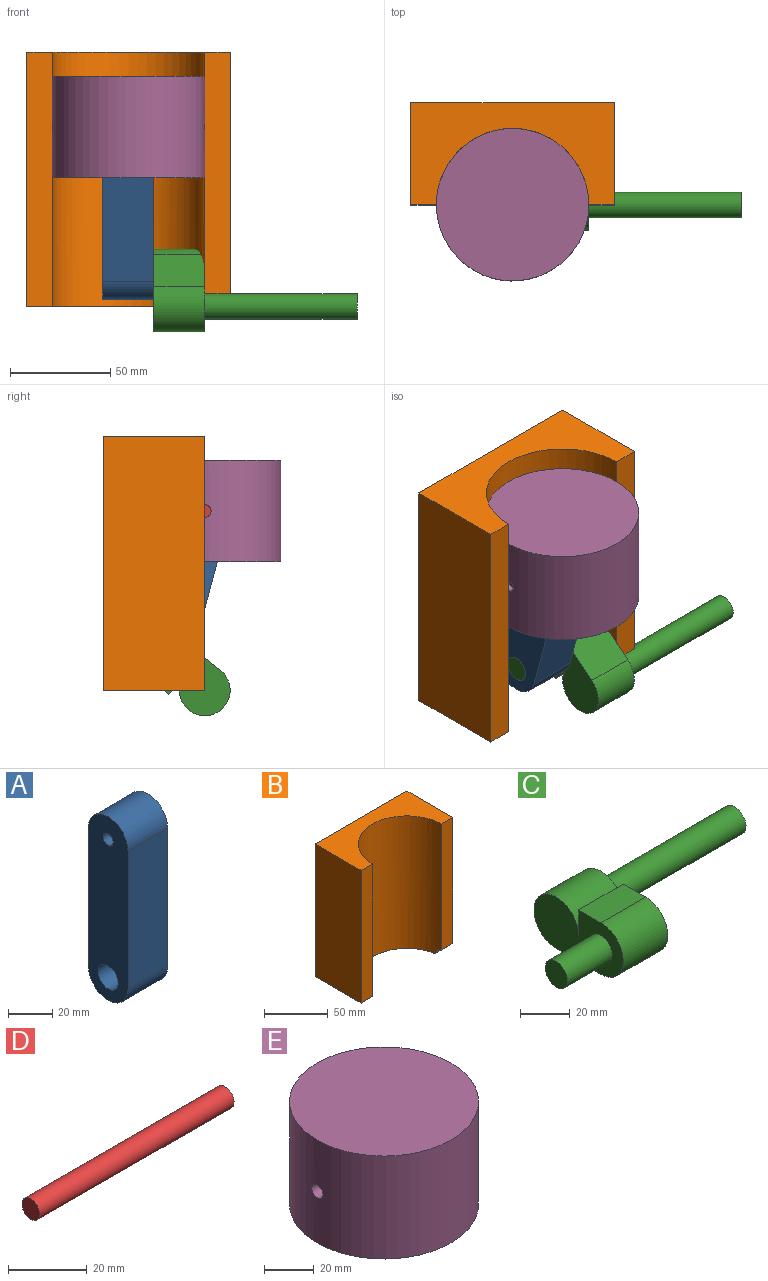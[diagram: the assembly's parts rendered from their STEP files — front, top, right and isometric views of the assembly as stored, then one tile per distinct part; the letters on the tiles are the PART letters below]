
ASSEMBLY  parts=5 mates=5
PART A: 8 faces, bbox 25.4x25.4x101.6 mm
  f0: plane 76.2x25.4mm, normal (0,1,0), area 1935.5mm2, adj f1,f4,f6,f7
  f1: cylinder r=12.7mm len=25.4mm, axis (1,0,0), area 1013.4mm2, adj f0,f2,f6,f7
  f2: plane 76.2x25.4mm, normal (0,-1,0), area 1935.5mm2, adj f1,f4,f6,f7
  f3: cylinder r=6.35mm len=25.4mm, axis (1,0,0), area 1013.4mm2, adj f6,f7
  f4: cylinder r=12.7mm len=25.4mm, axis (1,0,0), area 1013.4mm2, adj f0,f2,f6,f7
  f5: cylinder r=3.17mm len=25.4mm, axis (1,0,0), area 506.7mm2, adj f6,f7
  f6: plane 101.6x25.4mm, normal (-1,0,0), area 2283.8mm2, adj f0,f1,f2,f3,f4,f5
  f7: plane 101.6x25.4mm, normal (1,0,0), area 2283.8mm2, adj f0,f1,f2,f3,f4,f5
PART B: 10 faces, bbox 101.6x50.8x127 mm
  f0: cylinder r=38.1mm len=127mm, axis (0,0,1), area 15173mm2, adj f1,f2,f6,f7,f8
  f1: plane 120.65x12.7mm, normal (0,-1,0), area 1532.3mm2, adj f0,f3,f7,f9
  f2: plane 101.6x50.8mm, normal (0,0,-1), area 2799.5mm2, adj f0,f3,f4,f5,f6,f8,f9
  f3: plane 127x50.8mm, normal (1,0,0), area 6419.9mm2, adj f1,f2,f4,f7,f9
  f4: plane 127x101.6mm, normal (0,1,0), area 12903.2mm2, adj f2,f3,f5,f7
  f5: plane 127x50.8mm, normal (-1,0,0), area 6451.6mm2, adj f2,f4,f6,f7
  f6: plane 127x12.7mm, normal (0,-1,0), area 1612.9mm2, adj f0,f2,f5,f7
  f7: plane 101.6x50.8mm, normal (0,0,1), area 2881.1mm2, adj f0,f1,f3,f4,f5,f6
  f8: cone r=0mm half-angle=59deg, axis (1,0,0), area 4.1mm2, adj f0,f2,f9
  f9: cylinder r=6.35mm len=12.7mm, axis (1,0,0), area 126.7mm2, adj f1,f2,f3,f8
PART C: 11 faces, bbox 127x50.8x25.4 mm
  f0: cylinder r=12.7mm len=25.4mm, axis (-1,0,0), area 1520.1mm2, adj f1,f4,f5,f6
  f1: plane 25.4x12.7mm, normal (0,1,0), area 322.6mm2, adj f0,f2,f5,f6
  f2: plane 25.4x12.7mm, normal (0,0,1), area 322.6mm2, adj f1,f3,f5,f6
  f3: cylinder r=12.7mm len=25.4mm, axis (-1,0,0), area 1013.4mm2, adj f2,f4,f5,f6
  f4: plane 25.4x25.4mm, normal (0,0,-1), area 645.2mm2, adj f0,f3,f5,f6
  f5: plane 50.8x25.4mm, normal (1,0,0), area 990.6mm2, adj f0,f1,f2,f3,f4,f9
  f6: plane 50.8x25.4mm, normal (-1,0,0), area 990.6mm2, adj f0,f1,f2,f3,f4,f7
  f7: cylinder r=6.35mm len=25.4mm, axis (1,0,0), area 1013.4mm2, adj f6,f8
  f8: plane 12.7x12.7mm, normal (-1,0,0), area 126.7mm2, adj f7
  f9: cylinder r=6.35mm len=76.2mm, axis (-1,0,0), area 3040.2mm2, adj f5,f10
  f10: plane 12.7x12.7mm, normal (1,0,0), area 126.7mm2, adj f9
PART D: 3 faces, bbox 69.9x6.4x6.4 mm
  f0: cylinder r=3.17mm len=69.85mm, axis (-1,0,0), area 1393.4mm2, adj f1,f2
  f1: plane 6.35x6.35mm, normal (1,0,0), area 31.7mm2, adj f0
  f2: plane 6.35x6.35mm, normal (-1,0,0), area 31.7mm2, adj f0
PART E: 7 faces, bbox 76.2x76.2x50.8 mm
  f0: cylinder r=38.1mm len=76.2mm, axis (0,0,1), area 12097.7mm2, adj f2,f3,f5,f6
  f1: cylinder r=31.75mm len=63.5mm, axis (0,0,1), area 8804.1mm2, adj f2,f4,f5,f6
  f2: plane 76.2x76.2mm, normal (0,0,-1), area 1393.4mm2, adj f0,f1
  f3: plane 76.2x76.2mm, normal (0,0,1), area 4560.4mm2, adj f0
  f4: plane 63.5x63.5mm, normal (0,0,-1), area 3166.9mm2, adj f1
  f5: cylinder r=3.17mm len=6.51mm, axis (1,0,0), area 126.9mm2, adj f0,f1
  f6: cylinder r=3.17mm len=6.51mm, axis (-1,0,0), area 126.9mm2, adj f0,f1
PLACE A rot(axis=(1,0,0),15deg) t=(-63.58,-70.09,-12.92)mm
PLACE B t=(-63.5,-63.5,0)mm fixed
PLACE C rot(axis=(-1,0,0),141.1deg) t=(-63.58,20.1,-190.08)mm
PLACE D rot(axis=(-1,0,0),8.7deg) t=(-63.58,-59.66,-12.34)mm
PLACE E t=(-63.5,-63.5,-12.05)mm
MATE revolute A.f5 <-> D.f0  axis (1,0,0) through (-63.58,-63.5,-37.45)mm
MATE cylindrical B.f8 <-> C.f0  axis (1,0,0) through (-12.7,-63.5,-127)mm
MATE slider E.f0 <-> B.f0  axis (0,0,1) through (-63.5,-63.5,-12.05)mm
MATE revolute D.f0 <-> E.f5  axis (1,0,0) through (-28.65,-63.5,-37.45)mm
MATE revolute C.f7 <-> A.f3  axis (1,0,0) through (-76.28,-43.74,-111.04)mm
